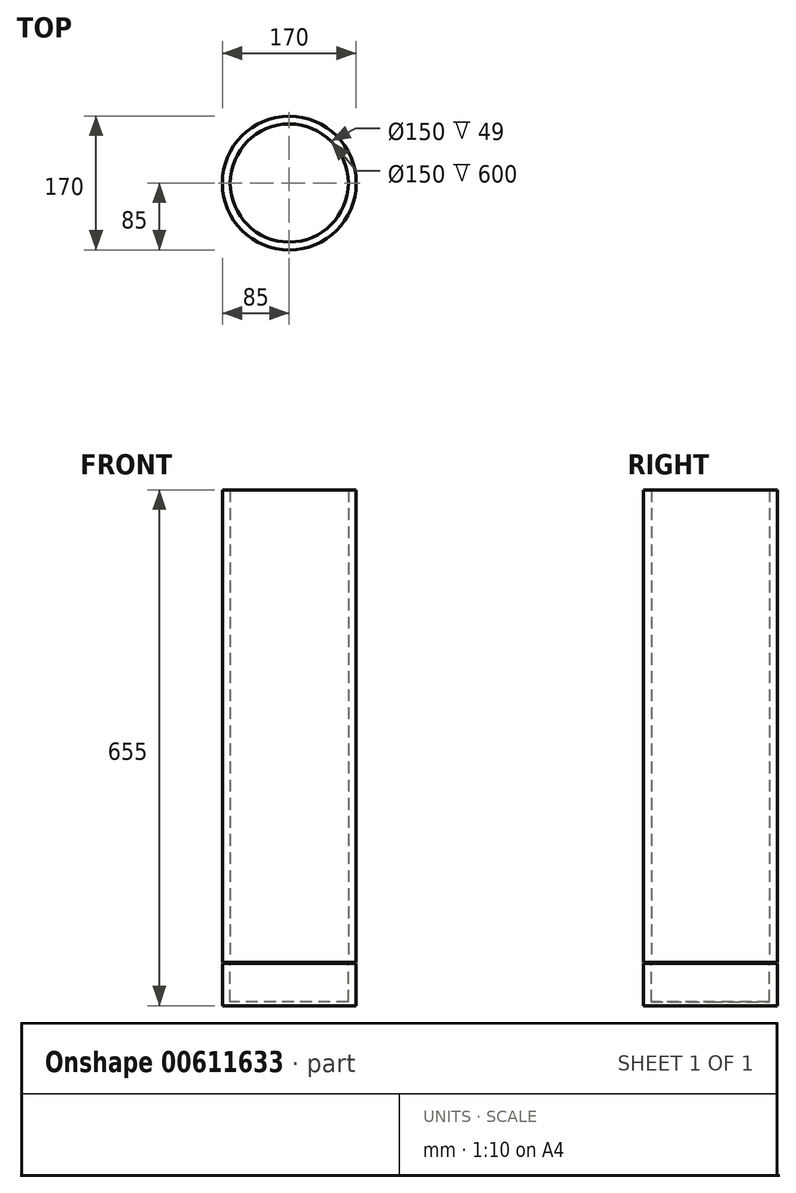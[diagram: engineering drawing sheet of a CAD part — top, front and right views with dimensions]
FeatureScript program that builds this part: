
annotation { "Feature Type Name" : "Feature", "Feature Type Description" : "" }
export const myFeature = defineFeature(function(context is Context, id is Id, definition is map)
    precondition{}
    {
        {
            var Q0;
            Q0=qCreatedBy(makeId("Top.planeOp"),FACE);
            var sketch = newSketch(context, id + "F0", { "sketchPlane" : qUnion([Q0])});
            skCircle(sketch, "E0", {"center": v(0, 0) * mm, "radius": 75 * mm});
            skCircle(sketch, "E1", {"center": v(0, 0) * mm, "radius": 85 * mm});
            skSolve(sketch);
        }
        {
            var Q0;
            Q0=makeQuery(id+"F0.imprint","IMPRINT",FACE,{"disambiguationData":[TD([[makeQuery(id+"F0.imprint","IMPRINT",EDGE,{"derivedFrom":sQuery(id+"F0.wireOp",EDGE,"E0")}),-1.0]])]});
            extrude(context, id + "F1", {"entities" : qUnion([Q0]), "depth" : 600 * mm, "offsetDistance" : 25 * mm});
        }
        {
            var Q0;
            Q0=makeQuery(id+"F1.opExtrude","CAP_FACE",FACE,{"disambiguationData":[OSD([sQuery(id+"F0.wireOp",EDGE,"E0"),sQuery(id+"F0.wireOp",EDGE,"E1")])],"isStart":true});
            extrude(context, id + "F2", {"entities" : qUnion([Q0]), "depth" : 50 * mm, "offsetDistance" : 25 * mm});
        }
        {
            var Q0;
            Q0=qCreatedBy(makeId("Right.planeOp"),FACE);
            var sketch = newSketch(context, id + "F3", { "sketchPlane" : qUnion([Q0])});
            skLineSegment(sketch, "E2.bottom", {"start": v(-86.87, 0) * mm, "end": v(88.13, 0) * mm});
            skLineSegment(sketch, "E2.top", {"start": v(-86.87, -1) * mm, "end": v(88.13, -1) * mm});
            skLineSegment(sketch, "E2.left", {"start": v(-86.87, 0) * mm, "end": v(-86.87, -1) * mm});
            skLineSegment(sketch, "E2.right", {"start": v(88.13, 0) * mm, "end": v(88.13, -1) * mm});
            skSolve(sketch);
        }
        {
            var Q0;
            Q0=makeQuery(id+"F3.imprint","IMPRINT",FACE,{"disambiguationData":[TD([[makeQuery(id+"F3.imprint","IMPRINT",EDGE,{"derivedFrom":sQuery(id+"F3.wireOp",EDGE,"E2.bottom")}),-1.0]])]});
            extrude(context, id + "F4", {"entities" : qUnion([Q0]), "operationType" : NewBodyOperationType.REMOVE, "oppositeDirection" : true, "depth" : 85.9 * mm, "offsetDistance" : 25 * mm, "hasSecondDirection" : true, "secondDirectionOppositeDirection" : false, "secondDirectionDepth" : 91.3 * mm});
        }
        {
            var Q0;
            Q0=makeQuery(id+"F2.opExtrude","CAP_FACE",FACE,{"disambiguationData":[OSD([sQuery(id+"F0.wireOp",EDGE,"E0"),sQuery(id+"F0.wireOp",EDGE,"E1")])],"isStart":false});
            var sketch = newSketch(context, id + "F5", { "sketchPlane" : qUnion([Q0])});
            skCircle(sketch, "E3", {"center": v(0, 0) * mm, "radius": 85 * mm});
            skSolve(sketch);
        }
        {
            var Q0;
            Q0 = qSketchRegion(id + "F5", true);
            extrude(context, id + "F6", {"entities" : qUnion([Q0]), "operationType" : NewBodyOperationType.ADD, "depth" : 5 * mm, "offsetDistance" : 25 * mm});
        }
    });
